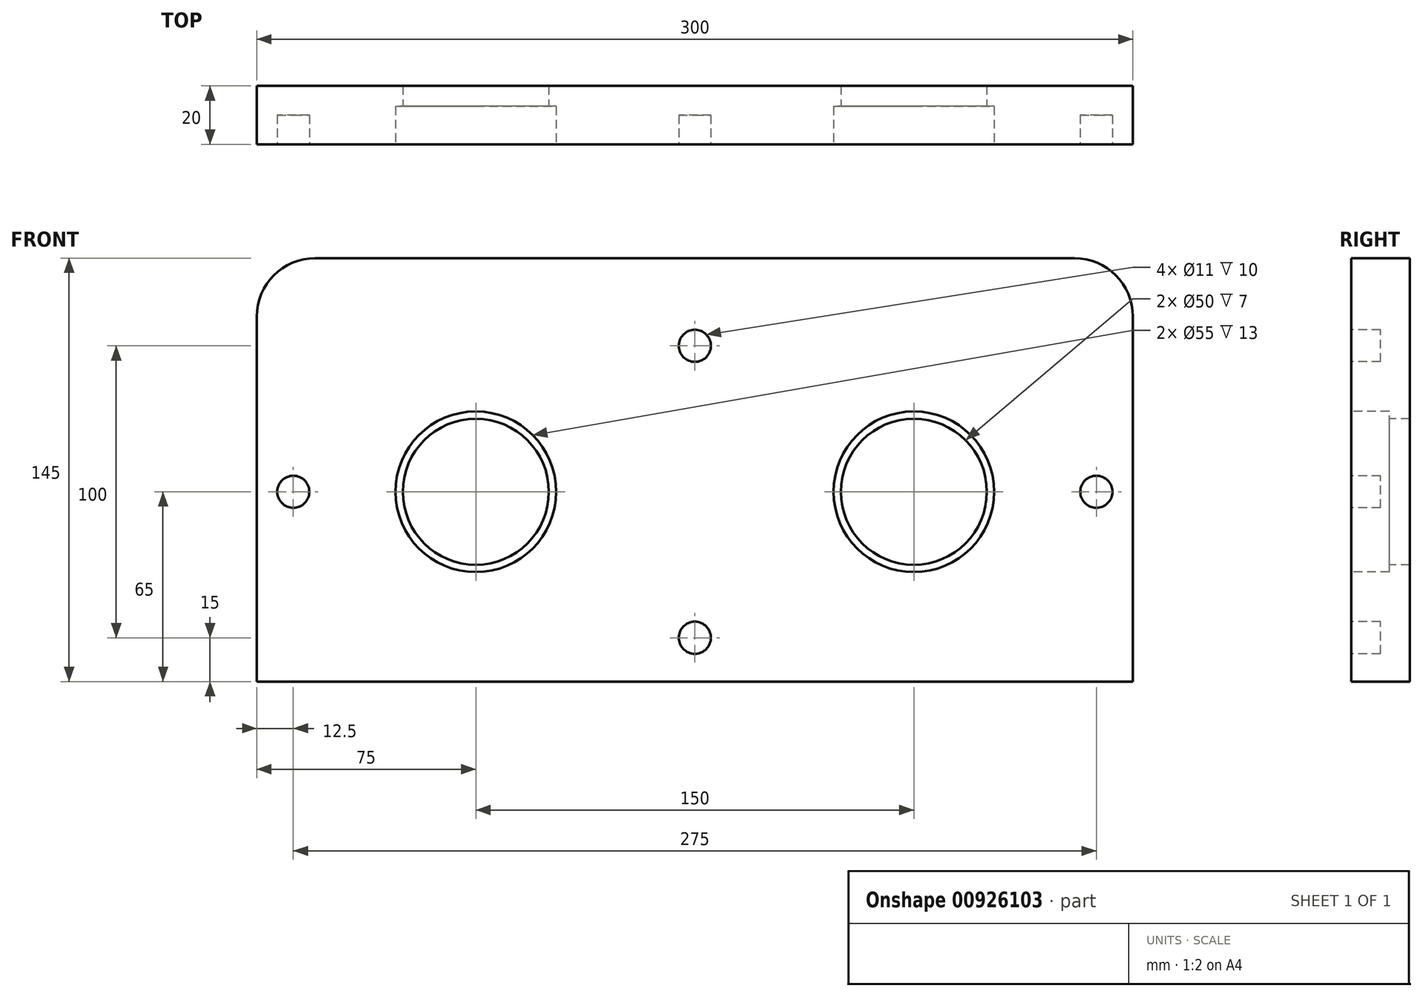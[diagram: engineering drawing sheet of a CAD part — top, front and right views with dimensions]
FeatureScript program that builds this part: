
annotation { "Feature Type Name" : "Feature", "Feature Type Description" : "" }
export const myFeature = defineFeature(function(context is Context, id is Id, definition is map)
    precondition{}
    {
        {
            var Q0;
            Q0=qCreatedBy(makeId("Front.planeOp"),FACE);
            var sketch = newSketch(context, id + "F0", { "sketchPlane" : qUnion([Q0])});
            skLineSegment(sketch, "E0.bottom", {"start": v(-150, 80) * mm, "end": v(150, 80) * mm});
            skLineSegment(sketch, "E0.top", {"start": v(-150, -80) * mm, "end": v(150, -80) * mm});
            skLineSegment(sketch, "E0.left", {"start": v(-150, 80) * mm, "end": v(-150, -80) * mm});
            skLineSegment(sketch, "E0.right", {"start": v(150, 80) * mm, "end": v(150, -80) * mm});
            skPoint(sketch, "E0.middle", {"position": v(0, 0) * mm});
            skSolve(sketch);
        }
        {
            var Q0;
            Q0=qSketchRegion(id+"F0",true);
            extrude(context, id + "F1", {"entities" : qUnion([Q0]), "endBound" : BoundingType.SYMMETRIC, "depth" : 20 * mm, "offsetDistance" : 25 * mm});
        }
        {
            var Q0;
            Q0=makeQuery(id+"F1.opExtrude","CAP_FACE",FACE,{"disambiguationData":[OSD([sQuery(id+"F0.wireOp",EDGE,"E0.bottom"),sQuery(id+"F0.wireOp",EDGE,"E0.top"),sQuery(id+"F0.wireOp",EDGE,"E0.left"),sQuery(id+"F0.wireOp",EDGE,"E0.right")])],"isStart":false});
            var sketch = newSketch(context, id + "F2", { "sketchPlane" : qUnion([Q0])});
            skCircle(sketch, "E1", {"center": v(-75, 0) * mm, "radius": 25 * mm});
            skCircle(sketch, "E2", {"center": v(75, 0) * mm, "radius": 25 * mm});
            skCircle(sketch, "E3", {"center": v(75, 0) * mm, "radius": 75 * mm, "construction": true});
            skCircle(sketch, "E4", {"center": v(-75, 0) * mm, "radius": 75 * mm, "construction": true});
            skSolve(sketch);
        }
        {
            var Q0;
            Q0=qSketchRegion(id+"F2",true);
            extrude(context, id + "F3", {"entities" : qUnion([Q0]), "operationType" : NewBodyOperationType.REMOVE, "endBound" : BoundingType.THROUGH_ALL, "oppositeDirection" : true, "depth" : 25 * mm, "offsetDistance" : 25 * mm});
        }
        {
            var Q0;
            Q0=makeQuery(id+"F1.opExtrude","CAP_FACE",FACE,{"disambiguationData":[OSD([sQuery(id+"F0.wireOp",EDGE,"E0.bottom"),sQuery(id+"F0.wireOp",EDGE,"E0.top"),sQuery(id+"F0.wireOp",EDGE,"E0.left"),sQuery(id+"F0.wireOp",EDGE,"E0.right")])],"isStart":false});
            var sketch = newSketch(context, id + "F4", { "sketchPlane" : qUnion([Q0])});
            skPoint(sketch, "E5", {"position": v(-137.5, 0) * mm});
            skPoint(sketch, "E6", {"position": v(137.5, 0) * mm});
            skPoint(sketch, "E7", {"position": v(0, 50) * mm});
            skPoint(sketch, "E8", {"position": v(0, -50) * mm});
            skLineSegment(sketch, "E9", {"start": v(-137.5, 0) * mm, "end": v(137.5, 0) * mm, "construction": true});
            skLineSegment(sketch, "E10", {"start": v(0, 50) * mm, "end": v(0, -50) * mm, "construction": true});
            skCircle(sketch, "E11", {"center": v(-137.5, 0) * mm, "radius": 5.5 * mm});
            skCircle(sketch, "E12", {"center": v(0, 50) * mm, "radius": 5.5 * mm});
            skCircle(sketch, "E13", {"center": v(137.5, 0) * mm, "radius": 5.5 * mm});
            skCircle(sketch, "E14", {"center": v(0, -50) * mm, "radius": 5.5 * mm});
            skSolve(sketch);
        }
        {
            var Q0;
            Q0=qSketchRegion(id+"F4",true);
            extrude(context, id + "F5", {"entities" : qUnion([Q0]), "operationType" : NewBodyOperationType.REMOVE, "oppositeDirection" : true, "depth" : 10 * mm, "offsetDistance" : 25 * mm});
        }
        {
            var Q0;
            Q0=makeQuery(id+"F1.opExtrude","CAP_FACE",FACE,{"disambiguationData":[OSD([sQuery(id+"F0.wireOp",EDGE,"E0.bottom"),sQuery(id+"F0.wireOp",EDGE,"E0.top"),sQuery(id+"F0.wireOp",EDGE,"E0.left"),sQuery(id+"F0.wireOp",EDGE,"E0.right")])],"isStart":false});
            var sketch = newSketch(context, id + "F6", { "sketchPlane" : qUnion([Q0])});
            skLineSegment(sketch, "E15.bottom", {"start": v(-150, -65) * mm, "end": v(150, -65) * mm});
            skLineSegment(sketch, "E15.top", {"start": v(-150, -80) * mm, "end": v(150, -80) * mm});
            skLineSegment(sketch, "E15.left", {"start": v(-150, -65) * mm, "end": v(-150, -80) * mm});
            skLineSegment(sketch, "E15.right", {"start": v(150, -65) * mm, "end": v(150, -80) * mm});
            skSolve(sketch);
        }
        {
            var Q0;
            Q0=qSketchRegion(id+"F6",true);
            extrude(context, id + "F7", {"entities" : qUnion([Q0]), "operationType" : NewBodyOperationType.REMOVE, "endBound" : BoundingType.THROUGH_ALL, "oppositeDirection" : true, "depth" : 25 * mm, "offsetDistance" : 25 * mm});
        }
        {
            var Q0;
            Q0=makeQuery(id+"F1.opExtrude","SWEPT_EDGE",EDGE,{"disambiguationData":[OSD([sQuery(id+"F0.wireOp",EDGE,"E0.bottom"),sQuery(id+"F0.wireOp",EDGE,"E0.left")])]});
            var Q1;
            Q1=makeQuery(id+"F1.opExtrude","SWEPT_EDGE",EDGE,{"disambiguationData":[OSD([sQuery(id+"F0.wireOp",EDGE,"E0.bottom"),sQuery(id+"F0.wireOp",EDGE,"E0.right")])]});
            var Q2;
            Q2=makeQuery(id+"F1.opExtrude","SWEPT_EDGE",EDGE,{"disambiguationData":[OSD([sQuery(id+"F0.wireOp",EDGE,"E0.top"),sQuery(id+"F0.wireOp",EDGE,"E0.left")])]});
            var Q3;
            Q3=makeQuery(id+"F1.opExtrude","SWEPT_EDGE",EDGE,{"disambiguationData":[OSD([sQuery(id+"F0.wireOp",EDGE,"E0.top"),sQuery(id+"F0.wireOp",EDGE,"E0.right")])]});
            var Q4;
            Q4=makeQuery(id+"F7.boolean.opBoolean","COPY",EDGE,{"derivedFrom":makeQuery(id+"F7.opExtrude","SWEPT_EDGE",EDGE,{"disambiguationData":[OSD([sQuery(id+"F0.wireOp",EDGE,"E0.left"),sQuery(id+"F6.wireOp",EDGE,"E15.bottom"),sQuery(id+"F6.wireOp",EDGE,"E15.left")])]})});
            var Q5;
            Q5=makeQuery(id+"F7.boolean.opBoolean","COPY",EDGE,{"derivedFrom":makeQuery(id+"F7.opExtrude","SWEPT_EDGE",EDGE,{"disambiguationData":[OSD([sQuery(id+"F0.wireOp",EDGE,"E0.right"),sQuery(id+"F6.wireOp",EDGE,"E15.bottom"),sQuery(id+"F6.wireOp",EDGE,"E15.right")])]})});
            fillet(context, id + "F8", {"entities" : qUnion([Q0, Q1, Q2, Q3, Q4, Q5]), "radius" : 20 * mm, "tangentPropagation" : true, "allowEdgeOverflow" : false});
        }
        {
            var Q0;
            Q0=makeQuery(id+"F1.opExtrude","CAP_FACE",FACE,{"disambiguationData":[OSD([sQuery(id+"F0.wireOp",EDGE,"E0.bottom"),sQuery(id+"F0.wireOp",EDGE,"E0.top"),sQuery(id+"F0.wireOp",EDGE,"E0.left"),sQuery(id+"F0.wireOp",EDGE,"E0.right")])],"isStart":false});
            var sketch = newSketch(context, id + "F9", { "sketchPlane" : qUnion([Q0])});
            skCircle(sketch, "E16", {"center": v(-75, 0) * mm, "radius": 27.5 * mm});
            skCircle(sketch, "E17", {"center": v(75, 0) * mm, "radius": 27.5 * mm});
            skSolve(sketch);
        }
        {
            var Q0;
            Q0 = qSketchRegion(id + "F9", true);
            extrude(context, id + "F10", {"entities" : qUnion([Q0]), "operationType" : NewBodyOperationType.REMOVE, "oppositeDirection" : true, "depth" : 13 * mm, "offsetDistance" : 25 * mm});
        }
    });
